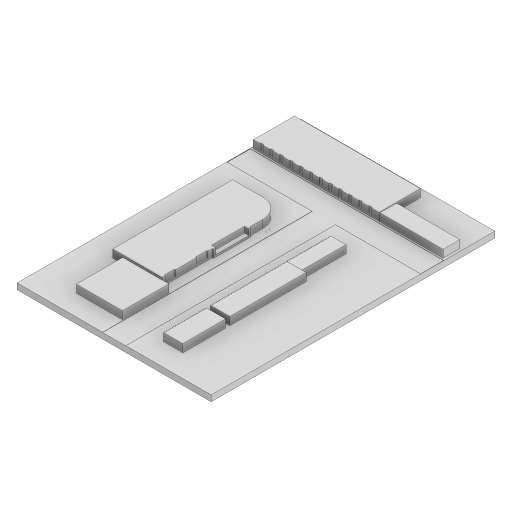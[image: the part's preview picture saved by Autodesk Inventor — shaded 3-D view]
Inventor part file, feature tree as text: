
AUTODESK INVENTOR PART (.ipt)
format: ipt  version: 2023 (Build 270158000, 158)  size: 550,400 bytes
history: native  units: in
note: dims shown in document units (in); Inventor stores cm internally (conversion verified against a paired STEP export)
features: projected_geometry x16, extrude x10, sketch x10, pattern_linear x3
ambient origin geometry x8: Origin, YZ Plane, XZ Plane, XY Plane, X Axis, Y Axis, Z Axis, Center Point
bodies: Solid1 (feature_tree)
feature tree (39):
  extrude  "Extrusion1"  Depth=472.4409in
  extrude  "Extrusion2"  Depth=3937.0079in
  extrude  "Extrusion3"  Depth=4.0in TaperAngle=0.0deg
  extrude  "Extrusion4"  Depth=157.4803in TaperAngle=0.0deg
  extrude  "Extrusion5"  Depth=118.1102in TaperAngle=0.0deg
  extrude  "Extrusion6"  Depth=118.1102in TaperAngle=0.0deg
  extrude  "Extrusion7"  Depth=39.3701in
  extrude  "Extrusion8"  Depth=78.7402in
  pattern_linear  "Rectangular Pattern1"  Count1=200 Spacing1=0.0in
  extrude  "Extrusion9"  Depth=118.1102in TaperAngle=0.0deg
  pattern_linear  "Rectangular Pattern2"  Count1=10 Spacing1=360.0in
  extrude  "Extrusion10"  Depth=60.0in
  pattern_linear  "Rectangular Pattern3"  [2 undecoded]
  sketch  "Sketch1"  dims[d0=1968.5039in d1=472.4409in]
  sketch  "Sketch2"  dims[d2=472.4409in d3=3937.0079in]
  projected_geometry  "Projected Loop1"
  sketch  "Sketch3"  dims[d4=1.0in d5=0.0in d6=4.0in d7=0.0in]
  projected_geometry  "Projected Loop2"
  sketch  "Sketch4"  dims[d8=393.7008in d9=157.4803in d10=0.0in]
  projected_geometry  "Projected Loop3"
  projected_geometry  "Projected Loop4"
  projected_geometry  "Projected Loop5"
  projected_geometry  "Projected Loop6"
  projected_geometry  "Projected Loop7"
  projected_geometry  "Projected Loop8"
  projected_geometry  "Projected Loop9"
  sketch  "Sketch5"  dims[d11=4.7244in d13=200.0in d14=0.3937in d16=1.0in d18=118.1102in d19=0.0in]
  projected_geometry  "Projected Loop10"
  sketch  "Sketch6"  dims[d20=118.1102in d21=0.0in d22=118.1102in d23=0.0in]
  projected_geometry  "Projected Loop11"
  projected_geometry  "Projected Loop12"
  sketch  "Sketch7"  dims[d24=39.3701in d25=0.0in d26=5.0in]
  projected_geometry  "Projected Loop13"
  sketch  "Sketch8"  dims[d27=5.0in d28=6.0in d29=78.7402in d30=0.0in]
  projected_geometry  "Projected Loop14"
  sketch  "Sketch9"  dims[d31=3.937in d33=240.0in d34=118.1102in d35=0.0in d36=3.937in d38=360.0in]
  sketch  "Sketch10"  dims[d39=118.1102in d40=0.0in d41=22.0472in d43=60.0in]
  projected_geometry  "Projected Loop15"
  projected_geometry  "Projected Loop16"
note: 2 required parameter values undecoded (feature->parameter linkage not recoverable at this tier; creation-order binding heuristic only, values carry confidence <= 0.55)
